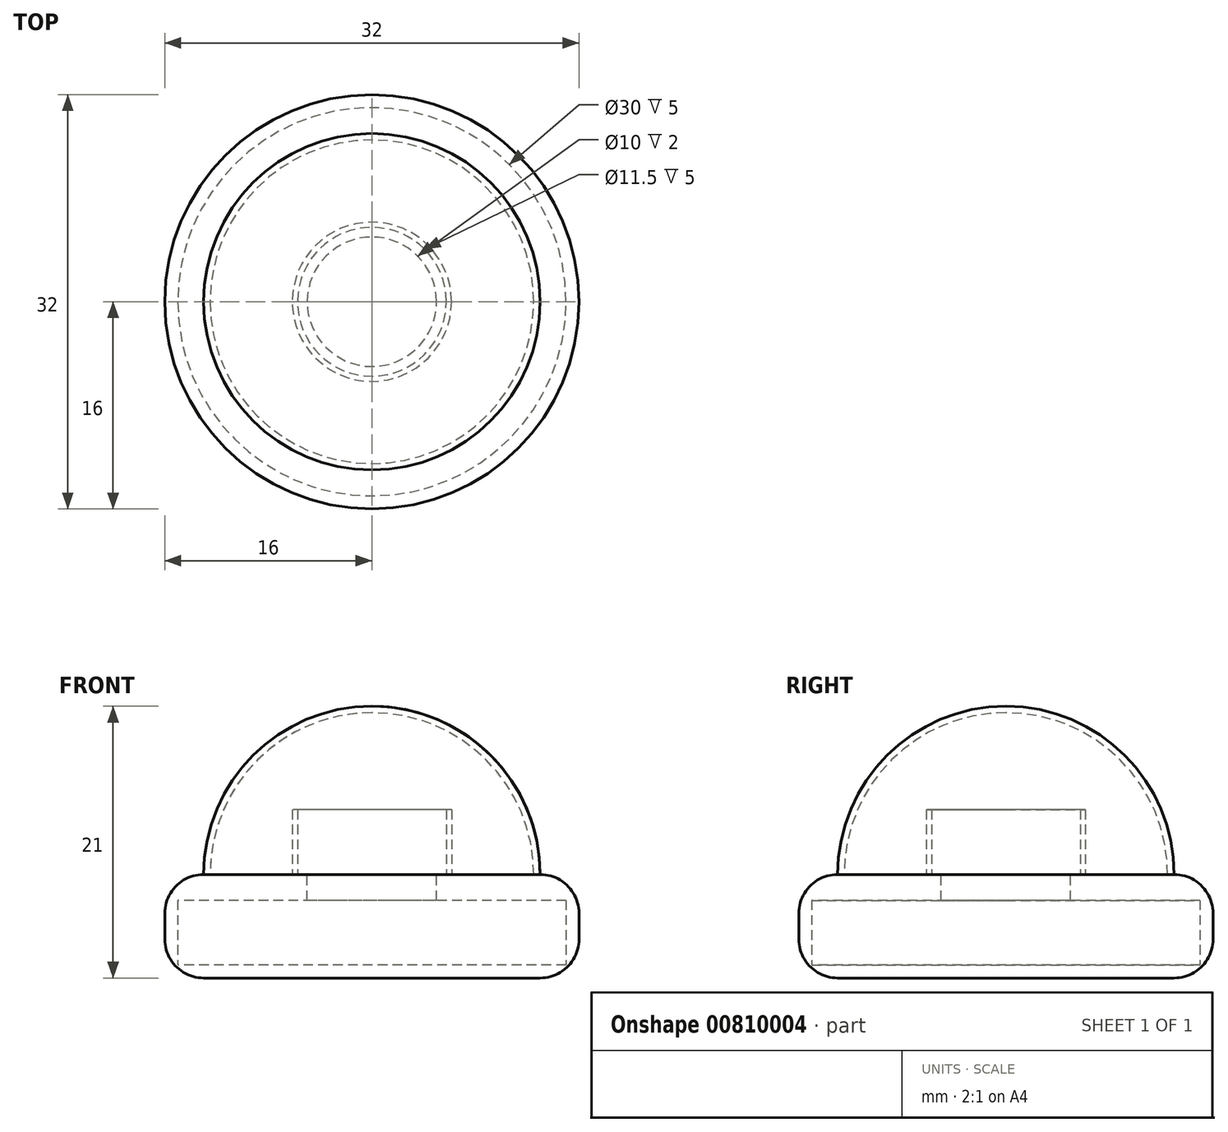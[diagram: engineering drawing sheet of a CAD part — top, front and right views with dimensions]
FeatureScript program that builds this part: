
annotation { "Feature Type Name" : "Feature", "Feature Type Description" : "" }
export const myFeature = defineFeature(function(context is Context, id is Id, definition is map)
    precondition{}
    {
        {
            var Q0;
            Q0=qCreatedBy(makeId("Top.planeOp"),FACE);
            var sketch = newSketch(context, id + "F0", { "sketchPlane" : qUnion([Q0])});
            skCircle(sketch, "E0", {"center": v(0, 0) * mm, "radius": 15 * mm});
            skCircle(sketch, "E1.0", {"center": v(0, 0) * mm, "radius": 16 * mm});
            skSolve(sketch);
        }
        {
            var Q0;
            Q0 = qSketchRegion(id + "F0", true);
            extrude(context, id + "F1", {"entities" : qUnion([Q0]), "depth" : 5 * mm, "offsetDistance" : 25 * mm});
        }
        {
            var Q0;
            Q0=makeQuery(id+"F1.opExtrude","CAP_FACE",FACE,{"disambiguationData":[OSD([sQuery(id+"F0.wireOp",EDGE,"E0"),sQuery(id+"F0.wireOp",EDGE,"E1.0")])],"isStart":false});
            var sketch = newSketch(context, id + "F2", { "sketchPlane" : qUnion([Q0])});
            skCircle(sketch, "E2", {"center": v(0, 0) * mm, "radius": 16 * mm});
            skSolve(sketch);
        }
        {
            var Q0;
            Q0 = qSketchRegion(id + "F2", true);
            extrude(context, id + "F3", {"entities" : qUnion([Q0]), "operationType" : NewBodyOperationType.ADD, "depth" : 2 * mm, "offsetDistance" : 25 * mm});
        }
        {
            var Q0;
            Q0=makeQuery(id+"F3.opExtrude","CAP_EDGE",EDGE,{"disambiguationData":[OSD([sQuery(id+"F2.wireOp",EDGE,"E2")])],"isStart":false});
            fillet(context, id + "F4", {"entities" : qUnion([Q0]), "radius" : 3 * mm, "tangentPropagation" : true, "allowEdgeOverflow" : false});
        }
        {
            var Q0;
            Q0=makeQuery(id+"F1.opExtrude","CAP_FACE",FACE,{"disambiguationData":[OSD([sQuery(id+"F0.wireOp",EDGE,"E0"),sQuery(id+"F0.wireOp",EDGE,"E1.0")])],"isStart":true});
            var sketch = newSketch(context, id + "F5", { "sketchPlane" : qUnion([Q0])});
            skCircle(sketch, "E3", {"center": v(0, 0) * mm, "radius": 16 * mm});
            skSolve(sketch);
        }
        {
            var Q0;
            Q0 = qSketchRegion(id + "F5", true);
            extrude(context, id + "F6", {"entities" : qUnion([Q0]), "operationType" : NewBodyOperationType.ADD, "depth" : 1 * mm, "offsetDistance" : 25 * mm});
        }
        {
            var Q0;
            Q0=makeQuery(id+"F6.opExtrude","CAP_EDGE",EDGE,{"disambiguationData":[OSD([sQuery(id+"F5.wireOp",EDGE,"E3")])],"isStart":false});
            fillet(context, id + "F7", {"entities" : qUnion([Q0]), "radius" : 3 * mm, "tangentPropagation" : true, "allowEdgeOverflow" : false});
        }
        {
            var Q0;
            Q0=makeQuery(id+"F3.opExtrude","CAP_FACE",FACE,{"disambiguationData":[OSD([sQuery(id+"F2.wireOp",EDGE,"E2")])],"isStart":false});
            var sketch = newSketch(context, id + "F8", { "sketchPlane" : qUnion([Q0])});
            skCircle(sketch, "E4", {"center": v(0, 0) * mm, "radius": 5 * mm});
            skSolve(sketch);
        }
        {
            var Q0;
            Q0 = qSketchRegion(id + "F8", true);
            extrude(context, id + "F9", {"entities" : qUnion([Q0]), "operationType" : NewBodyOperationType.REMOVE, "oppositeDirection" : true, "depth" : 7 * mm, "offsetDistance" : 25 * mm});
        }
        {
            var Q0;
            Q0=makeQuery(id+"F3.opExtrude","CAP_FACE",FACE,{"disambiguationData":[OSD([sQuery(id+"F2.wireOp",EDGE,"E2")])],"isStart":false});
            var sketch = newSketch(context, id + "F10", { "sketchPlane" : qUnion([Q0])});
            skCircle(sketch, "E5", {"center": v(0, 0) * mm, "radius": 5.75 * mm});
            skCircle(sketch, "E6.0", {"center": v(0, 0) * mm, "radius": 6.15 * mm});
            skSolve(sketch);
        }
        {
            var Q0;
            Q0 = qSketchRegion(id + "F10", true);
            extrude(context, id + "F11", {"entities" : qUnion([Q0]), "operationType" : NewBodyOperationType.ADD, "depth" : 5 * mm, "offsetDistance" : 25 * mm});
        }
        {
            var Q0;
            {var subQ0=sQuery(id+"F2.wireOp",EDGE,"E2");Q0=makeQuery(id+"F11.boolean.opBoolean","SPLIT",FACE,{"disambiguationData":[TD([makeQuery(id+"F4.opFillet","BLEND_FACE",FACE,{"disambiguationData":[OSD([subQ0])]})])],"derivedFrom":makeQuery(id+"F3.opExtrude","CAP_FACE",FACE,{"disambiguationData":[OSD([subQ0])],"isStart":false})});}
            var sketch = newSketch(context, id + "F12", { "sketchPlane" : qUnion([Q0])});
            skPoint(sketch, "E7", {"position": v(13, 0) * mm});
            skSolve(sketch);
        }
        {
            var Q0;
            Q0=qCreatedBy(makeId("Front.planeOp"),FACE);
            var sketch = newSketch(context, id + "F13", { "sketchPlane" : qUnion([Q0])});
            skArc(sketch, "E8", {"start": v(0, 20) * mm, "mid": v(-9.2, 16.2) * mm, "end": v(-13, 7) * mm});
            skLineSegment(sketch, "E9", {"start": v(0, 7) * mm, "end": v(0, 20) * mm});
            skPoint(sketch, "E10.orphan", {"position": v(13, 7) * mm});
            skArc(sketch, "E11.0", {"start": v(0, 19.5) * mm, "mid": v(-8.84, 15.84) * mm, "end": v(-12.5, 7) * mm});
            skLineSegment(sketch, "E12", {"start": v(-13, 7) * mm, "end": v(-12.5, 7) * mm});
            skSolve(sketch);
        }
        {
            var Q0;
            {var subQ0=sQuery(id+"F13.wireOp",EDGE,"E8");Q0=makeQuery(id+"F13.imprint","IMPRINT",FACE,{"disambiguationData":[TD([[makeQuery(id+"F13.imprint","IMPRINT",EDGE,{"derivedFrom":subQ0}),1.0]])]});}
            var Q1;
            Q1=sQuery(id+"F13.wireOp",EDGE,"E9");
            revolve(context, id + "F14", {"operationType" : NewBodyOperationType.ADD, "surfaceOperationType" : NewSurfaceOperationType.NEW, "entities" : qUnion([Q0]), "axis" : qUnion([Q1]), "revolveType" : RevolveType.FULL});
        }
    });
